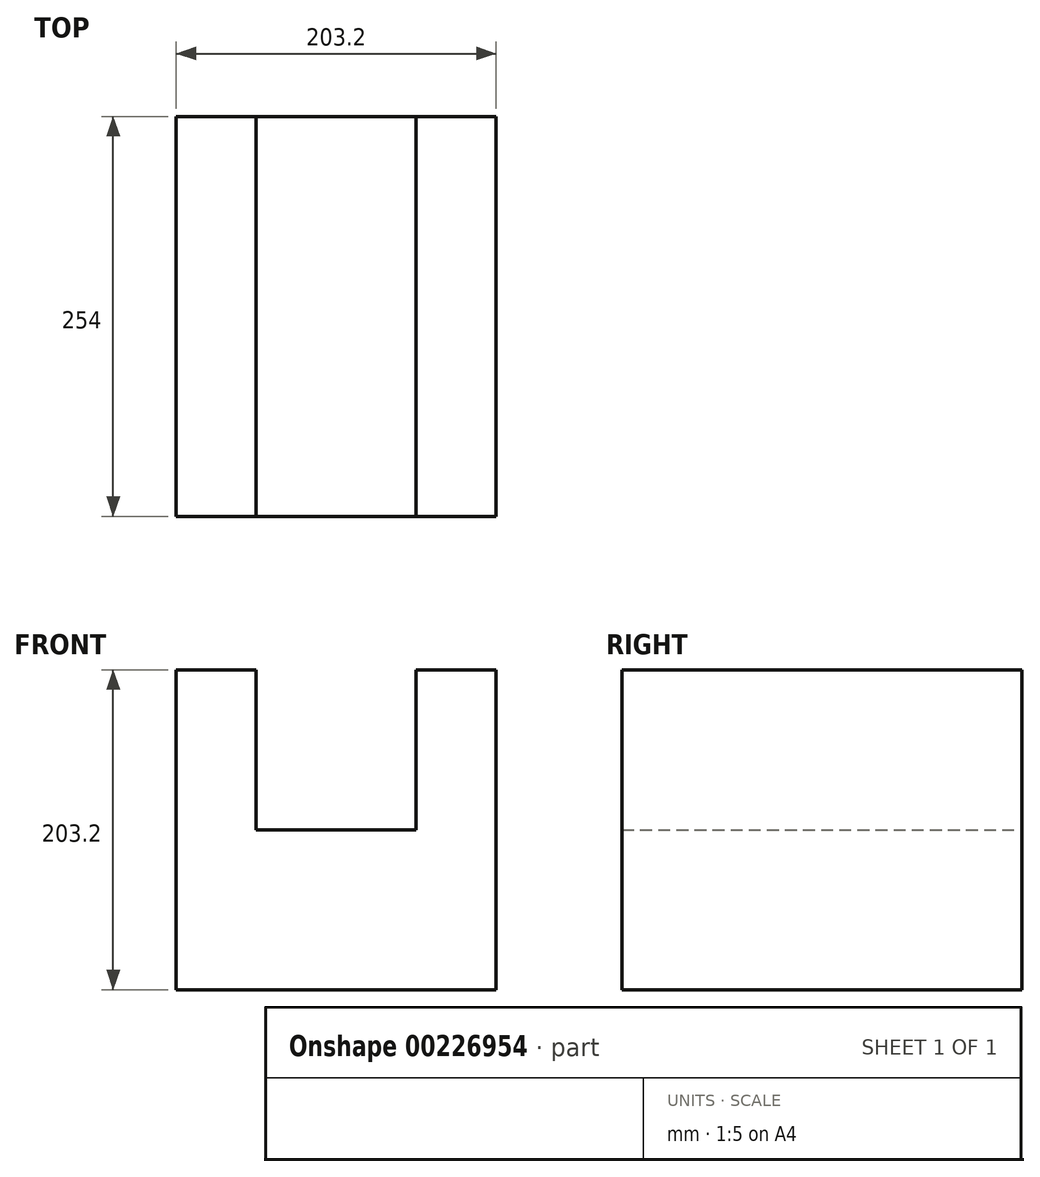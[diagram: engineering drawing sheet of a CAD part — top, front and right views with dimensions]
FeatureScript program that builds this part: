
annotation { "Feature Type Name" : "Feature", "Feature Type Description" : "" }
export const myFeature = defineFeature(function(context is Context, id is Id, definition is map)
    precondition{}
    {
        {
            var Q0;
            Q0=qCreatedBy(makeId("Front.planeOp"),FACE);
            var sketch = newSketch(context, id + "F0", { "sketchPlane" : qUnion([Q0])});
            skLineSegment(sketch, "E0.bottom", {"start": v(-98.43, -85.43) * mm, "end": v(104.77, -85.43) * mm});
            skLineSegment(sketch, "E0.left", {"start": v(-98.43, -85.43) * mm, "end": v(-98.43, 117.77) * mm});
            skLineSegment(sketch, "E0.right", {"start": v(104.77, -85.43) * mm, "end": v(104.77, 117.77) * mm});
            skLineSegment(sketch, "E1.top", {"start": v(-47.63, 16.17) * mm, "end": v(53.97, 16.17) * mm});
            skLineSegment(sketch, "E1.left", {"start": v(-47.63, 117.77) * mm, "end": v(-47.63, 16.17) * mm});
            skLineSegment(sketch, "E1.right", {"start": v(53.97, 117.77) * mm, "end": v(53.97, 16.17) * mm});
            skLineSegment(sketch, "E2", {"start": v(-98.43, 117.77) * mm, "end": v(-47.63, 117.77) * mm});
            skLineSegment(sketch, "E3", {"start": v(53.97, 117.77) * mm, "end": v(104.77, 117.77) * mm});
            skSolve(sketch);
        }
        {
            var Q0;
            Q0=makeQuery(id+"F0.imprint","IMPRINT",FACE,{"disambiguationData":[TD([[makeQuery(id+"F0.imprint","IMPRINT",EDGE,{"derivedFrom":sQuery(id+"F0.wireOp",EDGE,"E0.bottom")}),1.0]])]});
            extrude(context, id + "F1", {"entities" : qUnion([Q0]), "depth" : 254 * mm});
        }
    });
